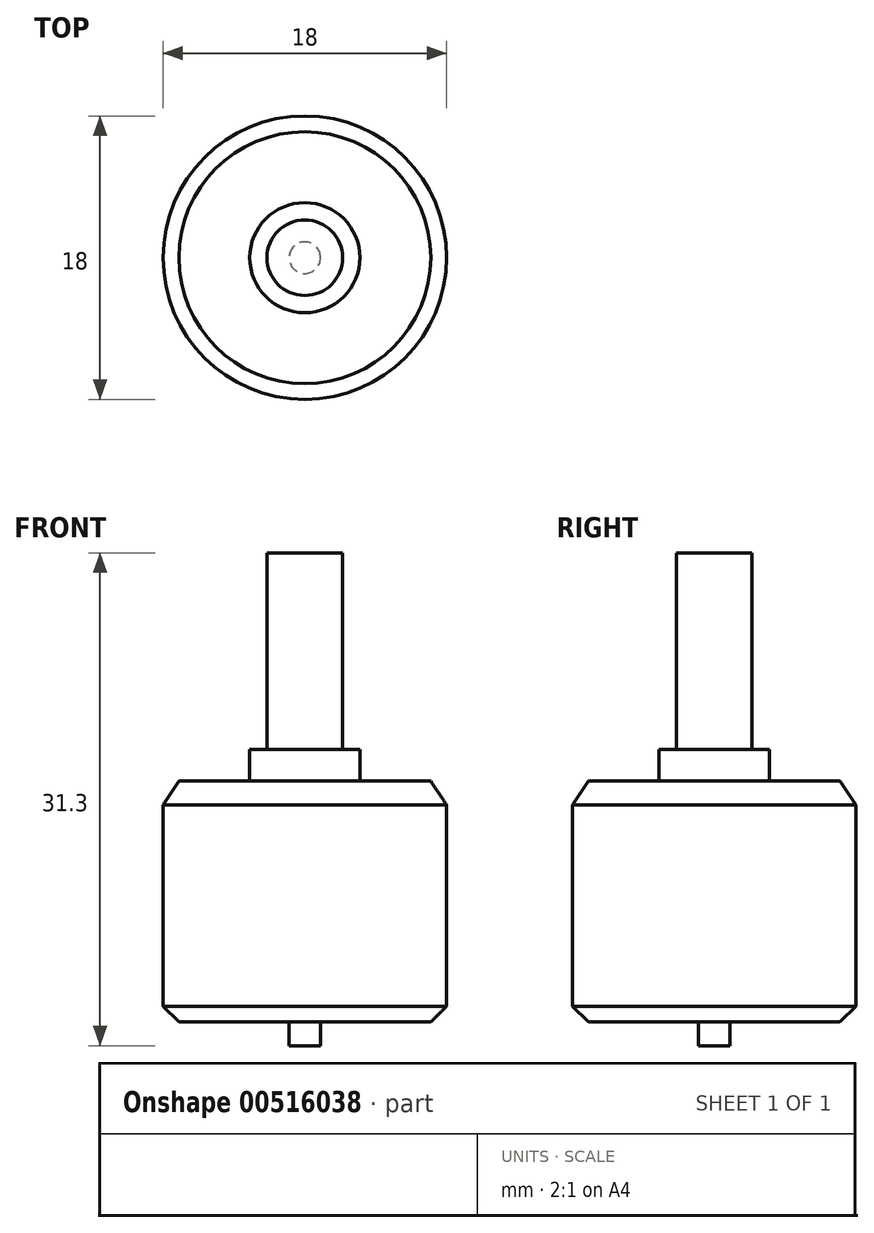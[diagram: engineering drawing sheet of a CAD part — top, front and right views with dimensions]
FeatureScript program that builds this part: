
annotation { "Feature Type Name" : "Feature", "Feature Type Description" : "" }
export const myFeature = defineFeature(function(context is Context, id is Id, definition is map)
    precondition{}
    {
        {
            var Q0;
            Q0=qCreatedBy(makeId("Top.planeOp"),FACE);
            var sketch = newSketch(context, id + "F0", { "sketchPlane" : qUnion([Q0])});
            skCircle(sketch, "E0", {"center": v(0, 0) * mm, "radius": 9 * mm});
            skSolve(sketch);
        }
        {
            var Q0;
            Q0 = qSketchRegion(id + "F0", true);
            extrude(context, id + "F1", {"entities" : qUnion([Q0]), "depth" : 15.3 * mm, "offsetDistance" : 25 * mm});
        }
        {
            var Q0;
            Q0=makeQuery(id+"F1.opExtrude","CAP_EDGE",EDGE,{"disambiguationData":[OSD([sQuery(id+"F0.wireOp",EDGE,"E0")])],"isStart":true});
            chamfer(context, id + "F2", {"entities" : qUnion([Q0]), "width" : 1 * mm, "tangentPropagation" : true});
        }
        {
            var Q0;
            Q0=makeQuery(id+"F1.opExtrude","CAP_EDGE",EDGE,{"disambiguationData":[OSD([sQuery(id+"F0.wireOp",EDGE,"E0")])],"isStart":false});
            chamfer(context, id + "F3", {"entities" : qUnion([Q0]), "chamferType" : ChamferType.TWO_OFFSETS, "width1" : 1 * mm, "oppositeDirection" : false, "width2" : 1.5 * mm, "tangentPropagation" : true});
        }
        {
            var Q0;
            Q0=makeQuery(id+"F1.opExtrude","CAP_FACE",FACE,{"disambiguationData":[OSD([sQuery(id+"F0.wireOp",EDGE,"E0")])],"isStart":false});
            var sketch = newSketch(context, id + "F4", { "sketchPlane" : qUnion([Q0])});
            skCircle(sketch, "E1", {"center": v(0, 0) * mm, "radius": 3.5 * mm});
            skSolve(sketch);
        }
        {
            var Q0;
            Q0 = qSketchRegion(id + "F4", true);
            extrude(context, id + "F5", {"entities" : qUnion([Q0]), "operationType" : NewBodyOperationType.ADD, "depth" : 2 * mm, "offsetDistance" : 25 * mm});
        }
        {
            var Q0;
            Q0=makeQuery(id+"F5.opExtrude","CAP_FACE",FACE,{"disambiguationData":[OSD([sQuery(id+"F4.wireOp",EDGE,"E1")])],"isStart":false});
            var sketch = newSketch(context, id + "F6", { "sketchPlane" : qUnion([Q0])});
            skCircle(sketch, "E2", {"center": v(0, 0) * mm, "radius": 2.4 * mm});
            skSolve(sketch);
        }
        {
            var Q0;
            Q0 = qSketchRegion(id + "F6", true);
            extrude(context, id + "F7", {"entities" : qUnion([Q0]), "operationType" : NewBodyOperationType.ADD, "depth" : 12.5 * mm, "offsetDistance" : 25 * mm});
        }
        {
            var Q0;
            Q0=makeQuery(id+"F1.opExtrude","CAP_FACE",FACE,{"disambiguationData":[OSD([sQuery(id+"F0.wireOp",EDGE,"E0")])],"isStart":true});
            var sketch = newSketch(context, id + "F8", { "sketchPlane" : qUnion([Q0])});
            skCircle(sketch, "E3", {"center": v(0, 0) * mm, "radius": 1 * mm});
            skSolve(sketch);
        }
        {
            var Q0;
            Q0 = qSketchRegion(id + "F8", true);
            extrude(context, id + "F9", {"entities" : qUnion([Q0]), "operationType" : NewBodyOperationType.ADD, "depth" : 1.5 * mm, "offsetDistance" : 25 * mm});
        }
    });
